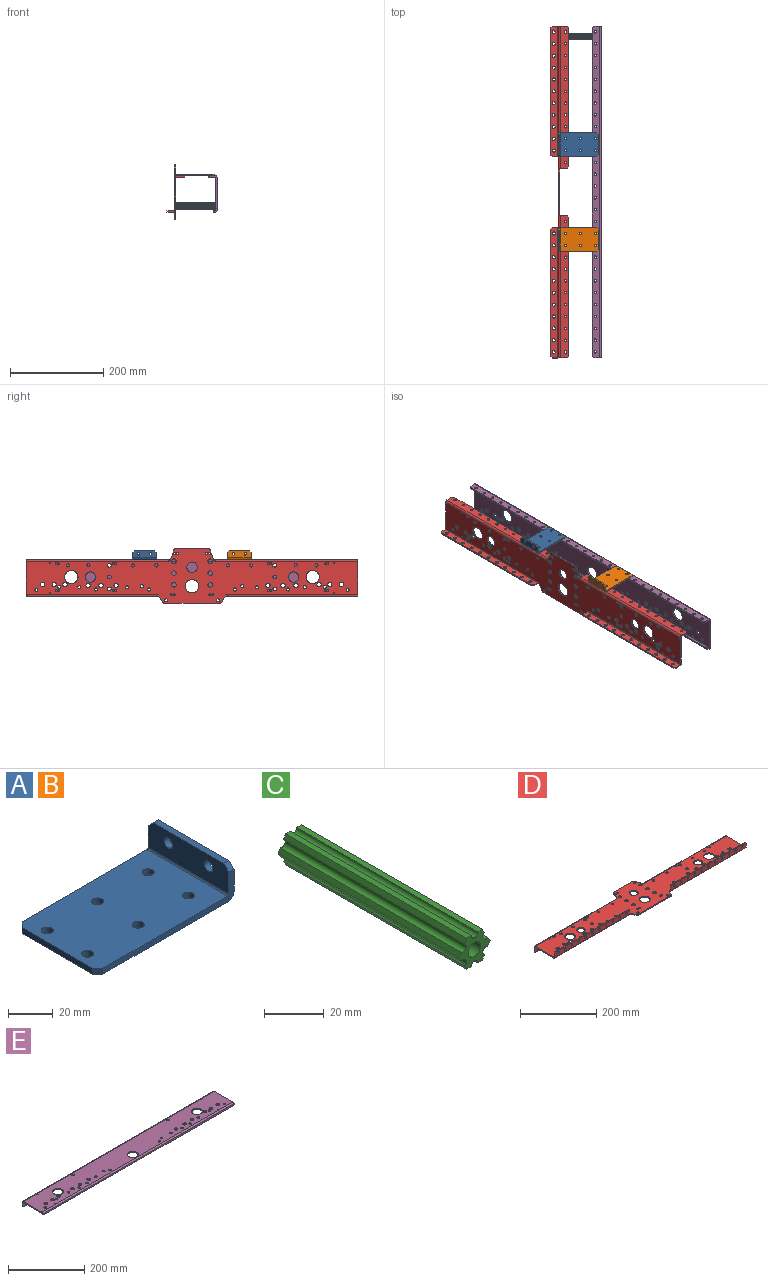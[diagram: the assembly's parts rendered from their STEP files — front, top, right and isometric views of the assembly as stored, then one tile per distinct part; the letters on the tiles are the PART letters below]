
ASSEMBLY  parts=5 mates=4
PART A: 22 faces, bbox 85.7x50.8x19.1 mm
  f0: cylinder r=2.67mm len=5.33mm, axis (-1,0,0), area 53.2mm2, adj f14,f15
  f1: cylinder r=2.67mm len=5.33mm, axis (-1,0,0), area 53.2mm2, adj f14,f15
  f2: cylinder r=2.67mm len=5.33mm, axis (0,0,1), area 53.2mm2, adj f10,f11
  f3: cylinder r=2.67mm len=5.33mm, axis (0,0,1), area 53.2mm2, adj f10,f11
  f4: cylinder r=2.67mm len=5.33mm, axis (0,0,1), area 53.2mm2, adj f10,f11
  f5: cylinder r=2.67mm len=5.33mm, axis (0,0,1), area 53.2mm2, adj f10,f11
  f6: cylinder r=2.67mm len=5.33mm, axis (0,0,1), area 53.2mm2, adj f10,f11
  f7: cylinder r=2.67mm len=5.33mm, axis (0,0,1), area 53.2mm2, adj f10,f11
  f8: plane 82.55x15.88mm, normal (0,1,0), area 299.2mm2, adj f10,f11,f12,f13,f14,f15,f18,f19
  f9: plane 44.45x3.18mm, normal (-1,0,0), area 141.1mm2, adj f10,f11,f19,f21
  f10: plane 81.79x50.8mm, normal (0,0,1), area 4010.7mm2, adj f2,f3,f4,f5,f6,f7,f8,f9
  f11: plane 81.79x50.8mm, normal (0,0,-1), area 4010.7mm2, adj f2,f3,f4,f5,f6,f7,f8,f9
  f12: cylinder r=3.94mm len=50.8mm, axis (0,1,0), area 314.2mm2, adj f8,f11,f14,f17
  f13: cylinder r=0.76mm len=50.8mm, axis (0,1,0), area 60.8mm2, adj f8,f10,f15,f17
  f14: plane 50.8x15.11mm, normal (1,0,0), area 713mm2, adj f0,f1,f8,f12,f16,f17,f18,f20
  f15: plane 50.8x15.11mm, normal (-1,0,0), area 713mm2, adj f0,f1,f8,f13,f16,f17,f18,f20
  f16: plane 44.45x3.18mm, normal (0,0,1), area 141.1mm2, adj f14,f15,f18,f20
  f17: plane 82.55x15.88mm, normal (0,-1,0), area 299.2mm2, adj f10,f11,f12,f13,f14,f15,f20,f21
  f18: plane 3.18x3.18mm, normal (0,0.71,0.71), area 14.3mm2, adj f8,f14,f15,f16
  f19: plane 3.18x3.18mm, normal (-0.71,0.71,0), area 14.3mm2, adj f8,f9,f10,f11
  f20: plane 3.18x3.18mm, normal (0,-0.71,0.71), area 14.3mm2, adj f14,f15,f16,f17
  f21: plane 3.18x3.18mm, normal (-0.71,-0.71,0), area 14.3mm2, adj f9,f10,f11,f17
PART B: same geometry as A
PART C: 21 faces, bbox 14.7x85.7x12.7 mm
  f0: cylinder r=2.93mm len=85.73mm, axis (0,1,0), area 1580.2mm2, adj f3,f4
  f1: cylinder r=1.59mm len=85.73mm, axis (0,1,0), area 427.5mm2, adj f3,f4,f5,f20
  f2: cylinder r=1.59mm len=85.73mm, axis (0,1,0), area 427.5mm2, adj f3,f4,f6,f7
  f3: plane 14.66x12.7mm, normal (0,-1,0), area 88.9mm2, adj f0,f1,f2,f5,f6,f7,f8,f9
  f4: plane 14.66x12.7mm, normal (0,1,0), area 88.9mm2, adj f0,f1,f2,f5,f6,f7,f8,f9
  f5: plane 85.73x1.8mm, normal (0.87,0,-0.5), area 178.2mm2, adj f1,f3,f4,f6
  f6: plane 85.73x1.8mm, normal (0.87,0,0.5), area 178.2mm2, adj f2,f3,f4,f5
  f7: plane 85.73x1.8mm, normal (0.87,0,0.5), area 178.2mm2, adj f2,f3,f4,f8
  f8: plane 85.73x2.08mm, normal (0,0,1), area 178.2mm2, adj f3,f4,f7,f9
  f9: cylinder r=1.59mm len=85.73mm, axis (0,1,0), area 427.5mm2, adj f3,f4,f8,f10
  f10: plane 85.73x2.08mm, normal (0,0,1), area 178.2mm2, adj f3,f4,f9,f11
  f11: plane 85.73x1.8mm, normal (-0.87,0,0.5), area 178.2mm2, adj f3,f4,f10,f12
  f12: cylinder r=1.59mm len=85.73mm, axis (0,1,0), area 427.5mm2, adj f3,f4,f11,f13
  f13: plane 85.73x1.8mm, normal (-0.87,0,0.5), area 178.2mm2, adj f3,f4,f12,f14
  f14: plane 85.73x1.8mm, normal (-0.87,0,-0.5), area 178.2mm2, adj f3,f4,f13,f15
  f15: cylinder r=1.59mm len=85.73mm, axis (0,1,0), area 427.5mm2, adj f3,f4,f14,f16
  f16: plane 85.73x1.8mm, normal (-0.87,0,-0.5), area 178.2mm2, adj f3,f4,f15,f17
  f17: plane 85.73x2.08mm, normal (0,0,-1), area 178.2mm2, adj f3,f4,f16,f18
  f18: cylinder r=1.59mm len=85.73mm, axis (0,1,0), area 427.5mm2, adj f3,f4,f17,f19
  f19: plane 85.73x2.08mm, normal (0,0,-1), area 178.2mm2, adj f3,f4,f18,f20
  f20: plane 85.73x1.8mm, normal (0.87,0,-0.5), area 178.2mm2, adj f1,f3,f4,f19
PART D: 190 faces, bbox 711.2x116.3x38.1 mm
  f0: cylinder r=3.35mm len=6.71mm, axis (0,0,1), area 66.9mm2, adj f128,f129
  f1: cylinder r=3.35mm len=6.71mm, axis (0,0,1), area 66.9mm2, adj f128,f129
  f2: cylinder r=3.35mm len=6.71mm, axis (0,0,1), area 66.9mm2, adj f128,f129
  f3: cylinder r=3.35mm len=6.71mm, axis (0,0,1), area 66.9mm2, adj f128,f129
  f4: cylinder r=3.35mm len=6.71mm, axis (0,0,1), area 66.9mm2, adj f128,f129
  f5: cylinder r=3.35mm len=6.71mm, axis (0,0,1), area 66.9mm2, adj f128,f129
  f6: cylinder r=3.35mm len=6.71mm, axis (0,0,1), area 66.9mm2, adj f128,f129
  f7: cylinder r=3.35mm len=6.71mm, axis (0,0,1), area 66.9mm2, adj f128,f129
  f8: cylinder r=3.35mm len=6.71mm, axis (0,0,1), area 66.9mm2, adj f128,f129
  f9: cylinder r=3.35mm len=6.71mm, axis (0,0,1), area 66.9mm2, adj f128,f129
  f10: cylinder r=2.55mm len=5.11mm, axis (0,0,1), area 50.9mm2, adj f128,f129
  f11: cylinder r=1.79mm len=3.57mm, axis (0,0,1), area 35.6mm2, adj f128,f129
  f12: cylinder r=2.55mm len=5.11mm, axis (0,0,1), area 50.9mm2, adj f128,f129
  f13: cylinder r=1.79mm len=3.57mm, axis (0,0,1), area 35.6mm2, adj f128,f129
  f14: cylinder r=14.29mm len=28.58mm, axis (0,0,1), area 285mm2, adj f128,f129
  f15: cylinder r=4.06mm len=8.13mm, axis (0,0,1), area 81.1mm2, adj f128,f129
  f16: cylinder r=1.79mm len=3.57mm, axis (0,0,1), area 35.6mm2, adj f128,f129
  f17: cylinder r=2.55mm len=5.11mm, axis (0,0,1), area 50.9mm2, adj f128,f129
  f18: cylinder r=11.11mm len=22.23mm, axis (0,0,1), area 221.7mm2, adj f128,f129
  f19: cylinder r=4.06mm len=8.13mm, axis (0,0,1), area 81.1mm2, adj f128,f129
  f20: cylinder r=4.06mm len=8.13mm, axis (0,0,1), area 81.1mm2, adj f128,f129
  f21: cylinder r=1.79mm len=3.57mm, axis (0,0,1), area 35.6mm2, adj f128,f129
  f22: cylinder r=2.55mm len=5.11mm, axis (0,0,1), area 50.9mm2, adj f128,f129
  f23: cylinder r=2.55mm len=5.11mm, axis (0,0,1), area 50.9mm2, adj f128,f129
  f24: cylinder r=1.79mm len=3.57mm, axis (0,0,1), area 35.6mm2, adj f128,f129
  f25: cylinder r=2.55mm len=5.11mm, axis (0,0,1), area 50.9mm2, adj f128,f129
  f26: cylinder r=1.79mm len=3.57mm, axis (0,0,1), area 35.6mm2, adj f128,f129
  f27: cylinder r=4.06mm len=8.13mm, axis (0,0,1), area 81.1mm2, adj f128,f129
  f28: cylinder r=4.06mm len=8.13mm, axis (0,0,1), area 81.1mm2, adj f128,f129
  f29: cylinder r=4.06mm len=8.13mm, axis (0,0,1), area 81.1mm2, adj f128,f129
  f30: cylinder r=11.11mm len=22.23mm, axis (0,0,1), area 221.7mm2, adj f128,f129
  f31: cylinder r=1.79mm len=3.57mm, axis (0,0,1), area 35.6mm2, adj f128,f129
  f32: cylinder r=2.55mm len=5.11mm, axis (0,0,1), area 50.9mm2, adj f128,f129
  f33: cylinder r=14.29mm len=28.58mm, axis (0,0,1), area 285mm2, adj f128,f129
  f34: cylinder r=1.79mm len=3.57mm, axis (0,0,1), area 35.6mm2, adj f128,f129
  f35: cylinder r=2.55mm len=5.11mm, axis (0,0,1), area 50.9mm2, adj f128,f129
  f36: cylinder r=3.4mm len=6.81mm, axis (0,0,1), area 67.9mm2, adj f128,f129
  f37: cylinder r=3.4mm len=6.81mm, axis (0,0,1), area 67.9mm2, adj f128,f129
  f38: cylinder r=1.27mm len=3.18mm, axis (0,0,-1), area 25.3mm2, adj f128,f129
  f39: cylinder r=1.27mm len=3.18mm, axis (0,0,-1), area 25.3mm2, adj f128,f129
  f40: cylinder r=1.27mm len=3.18mm, axis (0,0,-1), area 25.3mm2, adj f128,f129
  f41: cylinder r=1.27mm len=3.18mm, axis (0,0,-1), area 25.3mm2, adj f128,f129
  f42: cylinder r=3.35mm len=6.71mm, axis (0,0,-1), area 66.9mm2, adj f128,f129
  f43: cylinder r=3.35mm len=6.71mm, axis (0,0,-1), area 66.9mm2, adj f128,f129
  f44: cylinder r=3.35mm len=6.71mm, axis (0,0,-1), area 66.9mm2, adj f128,f129
  f45: cylinder r=3.35mm len=6.71mm, axis (0,0,-1), area 66.9mm2, adj f128,f129
  f46: cylinder r=3.35mm len=6.71mm, axis (0,0,-1), area 66.9mm2, adj f128,f129
  f47: cylinder r=3.35mm len=6.71mm, axis (0,0,-1), area 66.9mm2, adj f128,f129
  f48: cylinder r=2.03mm len=4.06mm, axis (0,0,-1), area 40.5mm2, adj f128,f129
  f49: cylinder r=2.03mm len=4.06mm, axis (0,0,-1), area 40.5mm2, adj f128,f129
  f50: cylinder r=2.54mm len=5.08mm, axis (0,0,-1), area 50.7mm2, adj f128,f129
  f51: cylinder r=2.54mm len=5.08mm, axis (0,0,-1), area 50.7mm2, adj f128,f129
  f52: cylinder r=2.03mm len=4.06mm, axis (0,0,-1), area 40.5mm2, adj f128,f129
  f53: cylinder r=2.03mm len=4.06mm, axis (0,0,-1), area 40.5mm2, adj f128,f129
  f54: cylinder r=2.54mm len=5.08mm, axis (0,0,-1), area 50.7mm2, adj f128,f129
  f55: cylinder r=2.54mm len=5.08mm, axis (0,0,-1), area 50.7mm2, adj f128,f129
  f56: cylinder r=4.76mm len=9.53mm, axis (0,0,-1), area 95mm2, adj f128,f129
  f57: cylinder r=4.76mm len=9.53mm, axis (0,0,-1), area 95mm2, adj f128,f129
  f58: cylinder r=4.76mm len=9.53mm, axis (0,0,-1), area 95mm2, adj f128,f129
  f59: cylinder r=4.76mm len=9.53mm, axis (0,0,-1), area 95mm2, adj f128,f129
  f60: cylinder r=4.76mm len=9.53mm, axis (0,0,-1), area 95mm2, adj f128,f129
  f61: cylinder r=4.76mm len=9.53mm, axis (0,0,-1), area 95mm2, adj f128,f129
  f62: cylinder r=11.11mm len=22.23mm, axis (0,0,-1), area 221.7mm2, adj f128,f129
  f63: cylinder r=3.35mm len=6.71mm, axis (0,1,0), area 66.9mm2, adj f148,f149
  f64: cylinder r=3.35mm len=6.71mm, axis (0,1,0), area 66.9mm2, adj f148,f149
  f65: cylinder r=3.35mm len=6.71mm, axis (0,1,0), area 66.9mm2, adj f148,f149
  f66: cylinder r=3.35mm len=6.71mm, axis (0,1,0), area 66.9mm2, adj f148,f149
  f67: cylinder r=3.35mm len=6.71mm, axis (0,1,0), area 66.9mm2, adj f148,f149
  f68: cylinder r=3.35mm len=6.71mm, axis (0,1,0), area 66.9mm2, adj f148,f149
  f69: cylinder r=3.35mm len=6.71mm, axis (0,1,0), area 66.9mm2, adj f148,f149
  f70: cylinder r=3.35mm len=6.71mm, axis (0,1,0), area 66.9mm2, adj f148,f149
  f71: cylinder r=3.35mm len=6.71mm, axis (0,1,0), area 66.9mm2, adj f148,f149
  f72: cylinder r=3.35mm len=6.71mm, axis (0,1,0), area 66.9mm2, adj f148,f149
  f73: cylinder r=3.35mm len=6.71mm, axis (0,1,0), area 66.9mm2, adj f148,f149
  f74: cylinder r=3.35mm len=6.71mm, axis (0,1,0), area 66.9mm2, adj f143,f144
  f75: cylinder r=3.35mm len=6.71mm, axis (0,1,0), area 66.9mm2, adj f143,f144
  f76: cylinder r=3.35mm len=6.71mm, axis (0,1,0), area 66.9mm2, adj f143,f144
  f77: cylinder r=3.35mm len=6.71mm, axis (0,1,0), area 66.9mm2, adj f143,f144
  f78: cylinder r=3.35mm len=6.71mm, axis (0,1,0), area 66.9mm2, adj f143,f144
  f79: cylinder r=3.35mm len=6.71mm, axis (0,1,0), area 66.9mm2, adj f143,f144
  f80: cylinder r=3.35mm len=6.71mm, axis (0,1,0), area 66.9mm2, adj f143,f144
  f81: cylinder r=3.35mm len=6.71mm, axis (0,1,0), area 66.9mm2, adj f143,f144
  f82: cylinder r=3.35mm len=6.71mm, axis (0,1,0), area 66.9mm2, adj f143,f144
  f83: cylinder r=3.35mm len=6.71mm, axis (0,1,0), area 66.9mm2, adj f143,f144
  f84: cylinder r=3.35mm len=6.71mm, axis (0,1,0), area 66.9mm2, adj f143,f144
  f85: cylinder r=2.67mm len=5.33mm, axis (0,1,0), area 53.2mm2, adj f136,f137
  f86: cylinder r=2.67mm len=5.33mm, axis (0,1,0), area 53.2mm2, adj f136,f137
  f87: cylinder r=2.67mm len=5.33mm, axis (0,1,0), area 53.2mm2, adj f136,f137
  f88: cylinder r=2.67mm len=5.33mm, axis (0,1,0), area 53.2mm2, adj f136,f137
  f89: cylinder r=2.67mm len=5.33mm, axis (0,1,0), area 53.2mm2, adj f136,f137
  f90: cylinder r=2.67mm len=5.33mm, axis (0,1,0), area 53.2mm2, adj f136,f137
  f91: cylinder r=2.67mm len=5.33mm, axis (0,1,0), area 53.2mm2, adj f136,f137
  f92: cylinder r=2.67mm len=5.33mm, axis (0,1,0), area 53.2mm2, adj f136,f137
  f93: cylinder r=2.67mm len=5.33mm, axis (0,1,0), area 53.2mm2, adj f136,f137
  f94: cylinder r=2.67mm len=5.33mm, axis (0,1,0), area 53.2mm2, adj f136,f137
  f95: cylinder r=2.67mm len=5.33mm, axis (0,1,0), area 53.2mm2, adj f136,f137
  f96: cylinder r=2.67mm len=5.33mm, axis (0,1,0), area 53.2mm2, adj f136,f137
  f97: cylinder r=2.67mm len=5.33mm, axis (0,1,0), area 53.2mm2, adj f153,f154
  f98: cylinder r=2.67mm len=5.33mm, axis (0,1,0), area 53.2mm2, adj f153,f154
  f99: cylinder r=2.67mm len=5.33mm, axis (0,1,0), area 53.2mm2, adj f153,f154
  f100: cylinder r=2.67mm len=5.33mm, axis (0,1,0), area 53.2mm2, adj f153,f154
  f101: cylinder r=2.67mm len=5.33mm, axis (0,1,0), area 53.2mm2, adj f153,f154
  f102: cylinder r=2.67mm len=5.33mm, axis (0,1,0), area 53.2mm2, adj f153,f154
  f103: cylinder r=2.67mm len=5.33mm, axis (0,1,0), area 53.2mm2, adj f153,f154
  f104: cylinder r=2.67mm len=5.33mm, axis (0,1,0), area 53.2mm2, adj f153,f154
  f105: cylinder r=2.67mm len=5.33mm, axis (0,1,0), area 53.2mm2, adj f153,f154
  f106: cylinder r=2.67mm len=5.33mm, axis (0,1,0), area 53.2mm2, adj f153,f154
  f107: cylinder r=2.67mm len=5.33mm, axis (0,1,0), area 53.2mm2, adj f153,f154
  f108: cylinder r=2.67mm len=5.33mm, axis (0,1,0), area 53.2mm2, adj f153,f154
  f109: cylinder r=3.35mm len=6.71mm, axis (0,0,1), area 66.9mm2, adj f128,f129
  f110: cylinder r=3.35mm len=6.71mm, axis (0,0,1), area 66.9mm2, adj f128,f129
  f111: cylinder r=3.35mm len=6.71mm, axis (0,0,1), area 66.9mm2, adj f128,f129
  f112: cylinder r=3.35mm len=6.71mm, axis (0,0,1), area 66.9mm2, adj f128,f129
  f113: cylinder r=3.35mm len=6.71mm, axis (0,0,1), area 66.9mm2, adj f128,f129
  f114: cylinder r=3.35mm len=6.71mm, axis (0,0,1), area 66.9mm2, adj f128,f129
  f115: cylinder r=4.83mm len=9.65mm, axis (0,0,1), area 96.3mm2, adj f128,f129
  f116: cylinder r=4.83mm len=9.65mm, axis (0,0,1), area 96.3mm2, adj f128,f129
  f117: cylinder r=4.83mm len=9.65mm, axis (0,0,1), area 96.3mm2, adj f128,f129
  f118: cylinder r=4.83mm len=9.65mm, axis (0,0,1), area 96.3mm2, adj f128,f129
  f119: cylinder r=4.83mm len=9.65mm, axis (0,0,1), area 96.3mm2, adj f128,f129
  f120: cylinder r=4.83mm len=9.65mm, axis (0,0,1), area 96.3mm2, adj f128,f129
  f121: cylinder r=4.83mm len=9.65mm, axis (0,0,1), area 96.3mm2, adj f128,f129
  f122: cylinder r=4.83mm len=9.65mm, axis (0,0,1), area 96.3mm2, adj f128,f129
  f123: cylinder r=4.83mm len=9.65mm, axis (0,0,1), area 96.3mm2, adj f128,f129
  f124: cylinder r=4.83mm len=9.65mm, axis (0,0,1), area 96.3mm2, adj f128,f129
  f125: cylinder r=4.83mm len=9.65mm, axis (0,0,1), area 96.3mm2, adj f128,f129
  f126: cylinder r=4.83mm len=9.65mm, axis (0,0,1), area 96.3mm2, adj f128,f129
  f127: cylinder r=14.29mm len=28.58mm, axis (0,0,1), area 285mm2, adj f128,f129
  f128: plane 711.2x116.33mm, normal (0,0,1), area 48642.2mm2, adj f0,f1,f2,f3,f4,f5,f6,f7
  f129: plane 711.2x116.33mm, normal (0,0,-1), area 48642.2mm2, adj f0,f1,f2,f3,f4,f5,f6,f7
  f130: plane 71.83x3.18mm, normal (0,1,0), area 228.1mm2, adj f128,f129,f169,f170
  f131: plane 120.39x3.18mm, normal (0,-1,0), area 382.2mm2, adj f128,f129,f173,f175
  f132: plane 3.18x0.91mm, normal (0,1,0), area 2.9mm2, adj f128,f129,f158,f168
  f133: plane 3.18x0.91mm, normal (0,1,0), area 2.9mm2, adj f128,f129,f159,f171
  f134: cylinder r=3.94mm len=304.8mm, axis (1,0,0), area 1885mm2, adj f128,f136,f158,f185
  f135: cylinder r=0.76mm len=304.8mm, axis (1,0,0), area 364.8mm2, adj f129,f137,f158,f185
  f136: plane 304.8x18.29mm, normal (0,1,0), area 5296mm2, adj f85,f86,f87,f88,f89,f90,f91,f92
  f137: plane 304.8x18.29mm, normal (0,-1,0), area 5296mm2, adj f85,f86,f87,f88,f89,f90,f91,f92
  f138: plane 298.45x3.18mm, normal (0,0,-1), area 947.6mm2, adj f136,f137,f179,f186
  f139: plane 3.18x1.34mm, normal (0,-1,0), area 4.3mm2, adj f128,f129,f156,f174
  f140: plane 3.18x1.34mm, normal (0,-1,0), area 4.3mm2, adj f128,f129,f157,f172
  f141: cylinder r=3.94mm len=279.4mm, axis (1,0,0), area 1727.9mm2, adj f129,f143,f156,f181
  f142: cylinder r=0.76mm len=279.4mm, axis (1,0,0), area 334.4mm2, adj f128,f144,f156,f181
  f143: plane 279.4x15.11mm, normal (0,-1,0), area 3824mm2, adj f74,f75,f76,f77,f78,f79,f80,f81
  f144: plane 279.4x15.11mm, normal (0,1,0), area 3824mm2, adj f74,f75,f76,f77,f78,f79,f80,f81
  f145: plane 273.05x3.18mm, normal (0,0,1), area 866.9mm2, adj f143,f144,f176,f189
  f146: cylinder r=3.94mm len=279.4mm, axis (1,0,0), area 1727.9mm2, adj f129,f148,f157,f183
  f147: cylinder r=0.76mm len=279.4mm, axis (1,0,0), area 334.4mm2, adj f128,f149,f157,f183
  f148: plane 279.4x15.11mm, normal (0,-1,0), area 3824mm2, adj f63,f64,f65,f66,f67,f68,f69,f70
  f149: plane 279.4x15.11mm, normal (0,1,0), area 3824mm2, adj f63,f64,f65,f66,f67,f68,f69,f70
  f150: plane 273.05x3.18mm, normal (0,0,1), area 866.9mm2, adj f148,f149,f177,f187
  f151: cylinder r=3.94mm len=304.8mm, axis (1,0,0), area 1885mm2, adj f128,f153,f159,f182
  f152: cylinder r=0.76mm len=304.8mm, axis (1,0,0), area 364.8mm2, adj f129,f154,f159,f182
  f153: plane 304.8x18.29mm, normal (0,1,0), area 5296mm2, adj f97,f98,f99,f100,f101,f102,f103,f104
  f154: plane 304.8x18.29mm, normal (0,-1,0), area 5296mm2, adj f97,f98,f99,f100,f101,f102,f103,f104
  f155: plane 298.45x3.18mm, normal (0,0,-1), area 947.6mm2, adj f153,f154,f178,f188
  f156: plane 15.88x3.94mm, normal (1,0,0), area 49.6mm2, adj f139,f141,f142,f143,f144,f176
  f157: plane 15.88x3.94mm, normal (-1,0,0), area 49.6mm2, adj f140,f146,f147,f148,f149,f177
  f158: plane 19.05x3.94mm, normal (-1,0,0), area 59.7mm2, adj f132,f134,f135,f136,f137,f179
  f159: plane 19.05x3.94mm, normal (1,0,0), area 59.7mm2, adj f133,f151,f152,f153,f154,f178
  f160: plane 15.88x9.17mm, normal (0.87,-0.5,0), area 58.2mm2, adj f128,f129,f172,f173
  f161: plane 15.88x9.17mm, normal (-0.87,-0.5,0), area 58.2mm2, adj f128,f129,f174,f175
  f162: plane 23.15x7.97mm, normal (-0.95,0.33,0), area 77.7mm2, adj f128,f129,f170,f171
  f163: plane 23.15x7.97mm, normal (0.95,0.33,0), area 77.7mm2, adj f128,f129,f168,f169
  f164: cylinder r=1.27mm len=3.18mm, axis (0,0,-1), area 12.7mm2, adj f128,f129,f180,f182
  f165: cylinder r=1.27mm len=3.18mm, axis (0,0,-1), area 12.7mm2, adj f128,f129,f180,f181
  f166: cylinder r=1.27mm len=3.18mm, axis (0,0,-1), area 12.7mm2, adj f128,f129,f184,f185
  f167: cylinder r=1.27mm len=3.18mm, axis (0,0,-1), area 12.7mm2, adj f128,f129,f183,f184
  f168: cylinder r=3.17mm len=3.18mm, axis (0,0,1), area 12.5mm2, adj f128,f129,f132,f163
  f169: cylinder r=3.17mm len=3.18mm, axis (0,0,-1), area 12.5mm2, adj f128,f129,f130,f163
  f170: cylinder r=3.17mm len=3.18mm, axis (0,0,-1), area 12.5mm2, adj f128,f129,f130,f162
  f171: cylinder r=3.17mm len=3.18mm, axis (0,0,-1), area 12.5mm2, adj f128,f129,f133,f162
  f172: cylinder r=3.17mm len=3.18mm, axis (0,0,-1), area 10.6mm2, adj f128,f129,f140,f160
  f173: cylinder r=3.17mm len=3.18mm, axis (0,0,-1), area 10.6mm2, adj f128,f129,f131,f160
  f174: cylinder r=3.17mm len=3.18mm, axis (0,0,1), area 10.6mm2, adj f128,f129,f139,f161
  f175: cylinder r=3.17mm len=3.18mm, axis (0,0,-1), area 10.6mm2, adj f128,f129,f131,f161
  f176: plane 3.18x3.18mm, normal (0.71,0,0.71), area 14.3mm2, adj f143,f144,f145,f156
  f177: plane 3.18x3.18mm, normal (-0.71,0,0.71), area 14.3mm2, adj f148,f149,f150,f157
  f178: plane 3.18x3.18mm, normal (0.71,0,-0.71), area 14.3mm2, adj f153,f154,f155,f159
  f179: plane 3.18x3.18mm, normal (-0.71,0,-0.71), area 14.3mm2, adj f136,f137,f138,f158
  f180: plane 60.96x3.18mm, normal (-1,0,0), area 193.5mm2, adj f128,f129,f164,f165
  f181: plane 15.88x5.84mm, normal (-1,0,0), area 55.7mm2, adj f128,f129,f141,f142,f143,f144,f165,f189
  f182: plane 19.05x5.84mm, normal (-1,0,0), area 65.7mm2, adj f128,f129,f151,f152,f153,f154,f164,f188
  f183: plane 15.88x5.84mm, normal (1,0,0), area 55.7mm2, adj f128,f129,f146,f147,f148,f149,f167,f187
  f184: plane 60.96x3.18mm, normal (1,0,0), area 193.5mm2, adj f128,f129,f166,f167
  f185: plane 19.05x5.84mm, normal (1,0,0), area 65.7mm2, adj f128,f129,f134,f135,f136,f137,f166,f186
  f186: plane 3.18x3.18mm, normal (0.71,0,-0.71), area 14.3mm2, adj f136,f137,f138,f185
  f187: plane 3.18x3.18mm, normal (0.71,0,0.71), area 14.3mm2, adj f148,f149,f150,f183
  f188: plane 3.18x3.18mm, normal (-0.71,0,-0.71), area 14.3mm2, adj f153,f154,f155,f182
  f189: plane 3.18x3.18mm, normal (-0.71,0,0.71), area 14.3mm2, adj f143,f144,f145,f181
PART E: 91 faces, bbox 711.2x77.7x19.1 mm
  f0: cylinder r=4.06mm len=8.13mm, axis (0,0,1), area 81.1mm2, adj f69,f70
  f1: cylinder r=4.06mm len=8.13mm, axis (0,0,1), area 81.1mm2, adj f69,f70
  f2: cylinder r=4.06mm len=8.13mm, axis (0,0,1), area 81.1mm2, adj f69,f70
  f3: cylinder r=4.06mm len=8.13mm, axis (0,0,1), area 81.1mm2, adj f69,f70
  f4: cylinder r=3.38mm len=6.76mm, axis (0,0,1), area 67.4mm2, adj f69,f70
  f5: cylinder r=3.38mm len=6.76mm, axis (0,0,1), area 67.4mm2, adj f69,f70
  f6: cylinder r=3.38mm len=6.76mm, axis (0,0,1), area 67.4mm2, adj f69,f70
  f7: cylinder r=3.38mm len=6.76mm, axis (0,0,1), area 67.4mm2, adj f69,f70
  f8: cylinder r=3.35mm len=6.71mm, axis (0,0,1), area 66.9mm2, adj f69,f70
  f9: cylinder r=3.35mm len=6.71mm, axis (0,0,1), area 66.9mm2, adj f69,f70
  f10: cylinder r=3.35mm len=6.71mm, axis (0,0,1), area 66.9mm2, adj f69,f70
  f11: cylinder r=3.35mm len=6.71mm, axis (0,0,1), area 66.9mm2, adj f69,f70
  f12: cylinder r=3.35mm len=6.71mm, axis (0,0,1), area 66.9mm2, adj f69,f70
  f13: cylinder r=3.35mm len=6.71mm, axis (0,0,1), area 66.9mm2, adj f69,f70
  f14: cylinder r=3.35mm len=6.71mm, axis (0,0,1), area 66.9mm2, adj f69,f70
  f15: cylinder r=3.35mm len=6.71mm, axis (0,0,1), area 66.9mm2, adj f69,f70
  f16: cylinder r=3.35mm len=6.71mm, axis (0,0,1), area 66.9mm2, adj f69,f70
  f17: cylinder r=3.35mm len=6.71mm, axis (0,0,1), area 66.9mm2, adj f69,f70
  f18: cylinder r=14.29mm len=28.58mm, axis (0,0,1), area 285mm2, adj f69,f70
  f19: cylinder r=14.29mm len=28.58mm, axis (0,0,1), area 285mm2, adj f69,f70
  f20: cylinder r=1.27mm len=3.18mm, axis (0,0,1), area 25.3mm2, adj f69,f70
  f21: cylinder r=1.27mm len=3.18mm, axis (0,0,1), area 25.3mm2, adj f69,f70
  f22: cylinder r=1.27mm len=3.18mm, axis (0,0,1), area 25.3mm2, adj f69,f70
  f23: cylinder r=1.27mm len=3.18mm, axis (0,0,1), area 25.3mm2, adj f69,f70
  f24: cylinder r=4.83mm len=9.65mm, axis (0,0,1), area 96.3mm2, adj f69,f70
  f25: cylinder r=4.83mm len=9.65mm, axis (0,0,1), area 96.3mm2, adj f69,f70
  f26: cylinder r=4.83mm len=9.65mm, axis (0,0,1), area 96.3mm2, adj f69,f70
  f27: cylinder r=4.83mm len=9.65mm, axis (0,0,1), area 96.3mm2, adj f69,f70
  f28: cylinder r=4.83mm len=9.65mm, axis (0,0,1), area 96.3mm2, adj f69,f70
  f29: cylinder r=4.83mm len=9.65mm, axis (0,0,1), area 96.3mm2, adj f69,f70
  f30: cylinder r=4.83mm len=9.65mm, axis (0,0,1), area 96.3mm2, adj f69,f70
  f31: cylinder r=4.83mm len=9.65mm, axis (0,0,1), area 96.3mm2, adj f69,f70
  f32: cylinder r=4.83mm len=9.65mm, axis (0,0,1), area 96.3mm2, adj f69,f70
  f33: cylinder r=4.83mm len=9.65mm, axis (0,0,1), area 96.3mm2, adj f69,f70
  f34: cylinder r=4.83mm len=9.65mm, axis (0,0,1), area 96.3mm2, adj f69,f70
  f35: cylinder r=4.83mm len=9.65mm, axis (0,0,1), area 96.3mm2, adj f69,f70
  f36: cylinder r=2.67mm len=5.33mm, axis (0,1,0), area 53.2mm2, adj f73,f74
  f37: cylinder r=2.67mm len=5.33mm, axis (0,1,0), area 53.2mm2, adj f73,f74
  f38: cylinder r=2.67mm len=5.33mm, axis (0,1,0), area 53.2mm2, adj f73,f74
  f39: cylinder r=2.67mm len=5.33mm, axis (0,1,0), area 53.2mm2, adj f73,f74
  f40: cylinder r=2.67mm len=5.33mm, axis (0,1,0), area 53.2mm2, adj f73,f74
  f41: cylinder r=2.67mm len=5.33mm, axis (0,1,0), area 53.2mm2, adj f73,f74
  f42: cylinder r=2.67mm len=5.33mm, axis (0,1,0), area 53.2mm2, adj f73,f74
  f43: cylinder r=2.67mm len=5.33mm, axis (0,1,0), area 53.2mm2, adj f73,f74
  f44: cylinder r=2.67mm len=5.33mm, axis (0,1,0), area 53.2mm2, adj f73,f74
  f45: cylinder r=2.67mm len=5.33mm, axis (0,1,0), area 53.2mm2, adj f73,f74
  f46: cylinder r=2.67mm len=5.33mm, axis (0,1,0), area 53.2mm2, adj f73,f74
  f47: cylinder r=2.67mm len=5.33mm, axis (0,1,0), area 53.2mm2, adj f73,f74
  f48: cylinder r=2.67mm len=5.33mm, axis (0,1,0), area 53.2mm2, adj f73,f74
  f49: cylinder r=2.67mm len=5.33mm, axis (0,1,0), area 53.2mm2, adj f73,f74
  f50: cylinder r=2.67mm len=5.33mm, axis (0,1,0), area 53.2mm2, adj f73,f74
  f51: cylinder r=2.67mm len=5.33mm, axis (0,1,0), area 53.2mm2, adj f73,f74
  f52: cylinder r=2.67mm len=5.33mm, axis (0,1,0), area 53.2mm2, adj f73,f74
  f53: cylinder r=2.67mm len=5.33mm, axis (0,1,0), area 53.2mm2, adj f73,f74
  f54: cylinder r=2.67mm len=5.33mm, axis (0,1,0), area 53.2mm2, adj f73,f74
  f55: cylinder r=2.67mm len=5.33mm, axis (0,1,0), area 53.2mm2, adj f73,f74
  f56: cylinder r=2.67mm len=5.33mm, axis (0,1,0), area 53.2mm2, adj f73,f74
  f57: cylinder r=2.67mm len=5.33mm, axis (0,1,0), area 53.2mm2, adj f73,f74
  f58: cylinder r=2.67mm len=5.33mm, axis (0,1,0), area 53.2mm2, adj f73,f74
  f59: cylinder r=2.67mm len=5.33mm, axis (0,1,0), area 53.2mm2, adj f73,f74
  f60: cylinder r=2.67mm len=5.33mm, axis (0,1,0), area 53.2mm2, adj f73,f74
  f61: cylinder r=2.67mm len=5.33mm, axis (0,1,0), area 53.2mm2, adj f73,f74
  f62: cylinder r=2.67mm len=5.33mm, axis (0,1,0), area 53.2mm2, adj f73,f74
  f63: cylinder r=2.67mm len=5.33mm, axis (0,1,0), area 53.2mm2, adj f73,f74
  f64: cylinder r=14.29mm len=28.58mm, axis (0,0,1), area 285mm2, adj f69,f70
  f65: plane 711.2x4mm, normal (0,-1,0), area 2835.1mm2, adj f67,f80,f81,f84,f87,f89
  f66: plane 711.2x4mm, normal (0,1,0), area 2835.1mm2, adj f68,f80,f81,f84,f87,f89
  f67: cylinder r=3.94mm len=711.2mm, axis (-1,0,0), area 4398.2mm2, adj f65,f69,f81,f84
  f68: cylinder r=0.76mm len=711.2mm, axis (-1,0,0), area 851.3mm2, adj f66,f70,f81,f84
  f69: plane 711.2x69.85mm, normal (0,0,1), area 46140.9mm2, adj f0,f1,f2,f3,f4,f5,f6,f7
  f70: plane 711.2x69.85mm, normal (0,0,-1), area 46140.9mm2, adj f0,f1,f2,f3,f4,f5,f6,f7
  f71: cylinder r=3.94mm len=711.2mm, axis (1,0,0), area 4398.2mm2, adj f69,f73,f83,f86
  f72: cylinder r=0.76mm len=711.2mm, axis (1,0,0), area 851.3mm2, adj f70,f74,f83,f86
  f73: plane 711.2x15.11mm, normal (0,1,0), area 10112.6mm2, adj f36,f37,f38,f39,f40,f41,f42,f43
  f74: plane 711.2x15.11mm, normal (0,-1,0), area 10112.6mm2, adj f36,f37,f38,f39,f40,f41,f42,f43
  f75: plane 704.85x3.18mm, normal (0,0,-1), area 2237.9mm2, adj f73,f74,f88,f90
  f76: cylinder r=1.27mm len=3.18mm, axis (0,0,1), area 12.7mm2, adj f69,f70,f82,f83
  f77: cylinder r=1.27mm len=3.18mm, axis (0,0,1), area 12.7mm2, adj f69,f70,f81,f82
  f78: cylinder r=1.27mm len=3.18mm, axis (0,0,1), area 12.7mm2, adj f69,f70,f85,f86
  f79: cylinder r=1.27mm len=3.18mm, axis (0,0,1), area 12.7mm2, adj f69,f70,f84,f85
  f80: plane 704.85x3.18mm, normal (0,0,-1), area 2237.9mm2, adj f65,f66,f87,f89
  f81: plane 5.84x4.76mm, normal (-1,0,0), area 20.4mm2, adj f65,f66,f67,f68,f69,f70,f77,f89
  f82: plane 60.96x3.18mm, normal (-1,0,0), area 193.5mm2, adj f69,f70,f76,f77
  f83: plane 15.88x5.84mm, normal (-1,0,0), area 55.7mm2, adj f69,f70,f71,f72,f73,f74,f76,f90
  f84: plane 5.84x4.76mm, normal (1,0,0), area 20.4mm2, adj f65,f66,f67,f68,f69,f70,f79,f87
  f85: plane 60.96x3.18mm, normal (1,0,0), area 193.5mm2, adj f69,f70,f78,f79
  f86: plane 15.88x5.84mm, normal (1,0,0), area 55.7mm2, adj f69,f70,f71,f72,f73,f74,f78,f88
  f87: plane 3.18x3.18mm, normal (0.71,0,-0.71), area 14.3mm2, adj f65,f66,f80,f84
  f88: plane 3.18x3.18mm, normal (0.71,0,-0.71), area 14.3mm2, adj f73,f74,f75,f86
  f89: plane 3.18x3.18mm, normal (-0.71,0,-0.71), area 14.3mm2, adj f65,f66,f80,f81
  f90: plane 3.18x3.18mm, normal (-0.71,0,-0.71), area 14.3mm2, adj f73,f74,f75,f83
PLACE A rot(axis=(0,0,1),180deg) t=(-6.35,139.7,56.51)mm
PLACE B rot(axis=(0,0,1),180deg) t=(-6.35,-63.5,56.51)mm
PLACE C rot(axis=(-0.58,0.58,0.58),120deg) t=(-88.9,333.38,-7.75)mm
PLACE D rot(axis=(0.58,-0.58,-0.58),120deg) t=(-80.04,284.95,40.73)mm
PLACE E rot(axis=(0.58,0.58,0.58),120deg) t=(-24.4,-283.95,32.92)mm
MATE fastened B.f6 <-> E.f53  axis (0,0,-1) through (-12.7,-88.9,56.52)mm
MATE fastened D.f9 <-> C.f0  axis (1,0,0) through (-88.9,333.38,-7.75)mm
MATE fastened C.f0 <-> E.f8  axis (1,0,0) through (-3.17,333.38,-7.75)mm
MATE fastened A.f6 <-> E.f45  axis (0,0,-1) through (-12.7,114.3,56.52)mm
